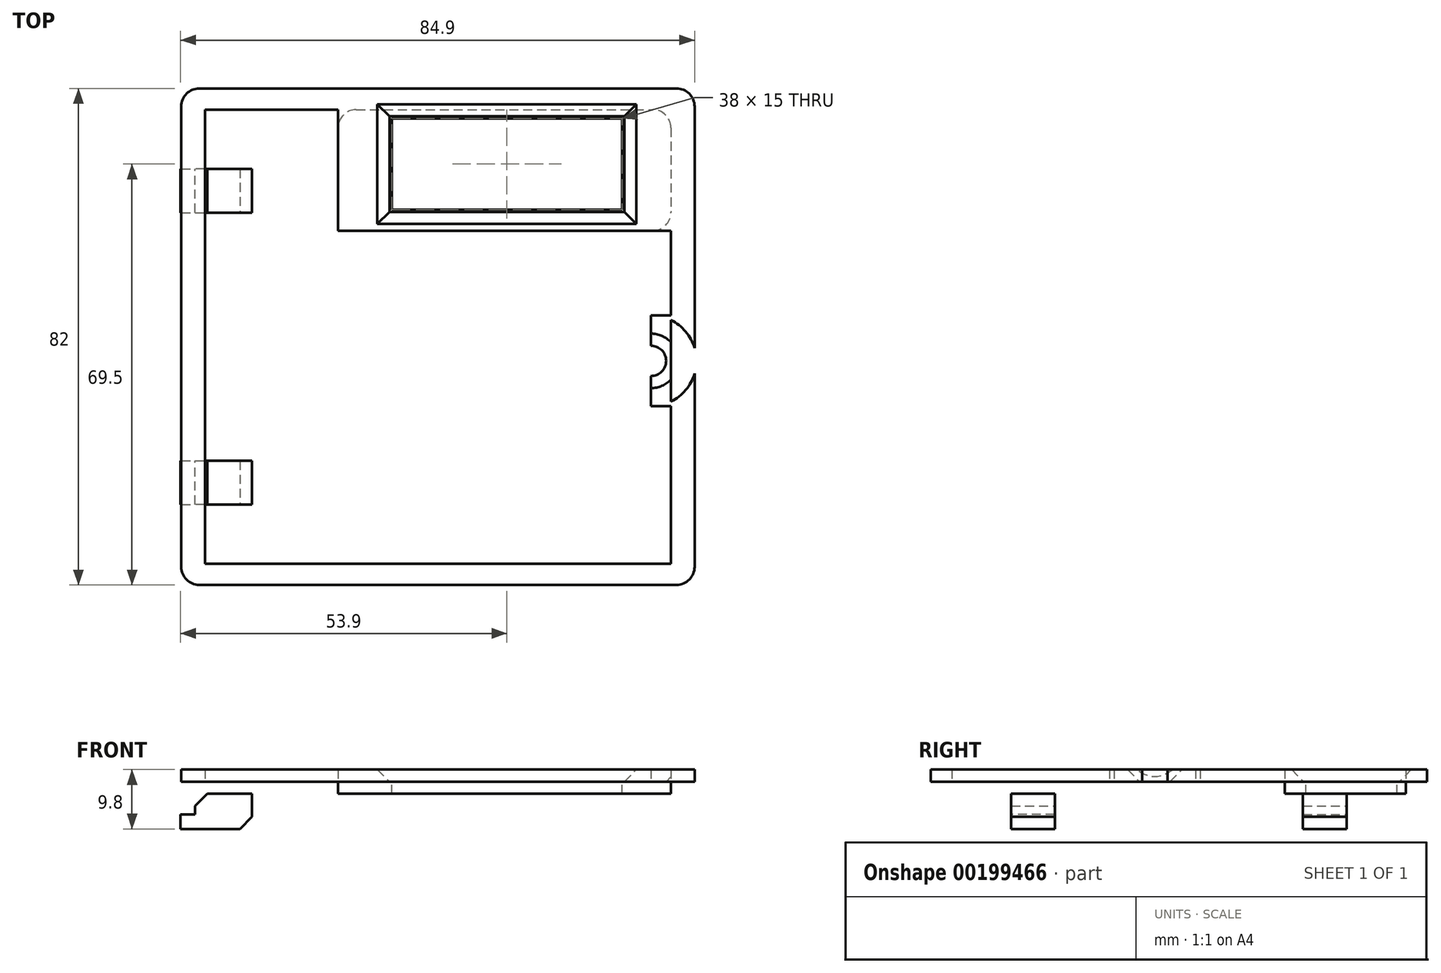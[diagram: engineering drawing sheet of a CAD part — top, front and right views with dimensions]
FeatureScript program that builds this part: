
annotation { "Feature Type Name" : "Feature", "Feature Type Description" : "" }
export const myFeature = defineFeature(function(context is Context, id is Id, definition is map)
    precondition{}
    {
        {
            var Q0;
            Q0=qCreatedBy(makeId("Top.planeOp"),FACE);
            var sketch = newSketch(context, id + "F0", { "sketchPlane" : qUnion([Q0])});
            skLineSegment(sketch, "E0.bottom", {"start": v(-34.8, 45) * mm, "end": v(50, 45) * mm});
            skLineSegment(sketch, "E0.top", {"start": v(-34.8, -37) * mm, "end": v(50, -37) * mm});
            skLineSegment(sketch, "E0.left", {"start": v(-34.8, 45) * mm, "end": v(-34.8, -37) * mm});
            skLineSegment(sketch, "E0.right", {"start": v(50, 45) * mm, "end": v(50, -37) * mm});
            skLineSegment(sketch, "E1.bottom", {"start": v(-30.9, 41.5) * mm, "end": v(46.1, 41.5) * mm});
            skLineSegment(sketch, "E1.top", {"start": v(-30.9, -33.5) * mm, "end": v(46.1, -33.5) * mm});
            skLineSegment(sketch, "E1.left", {"start": v(-30.9, 41.5) * mm, "end": v(-30.9, -33.5) * mm});
            skLineSegment(sketch, "E1.right", {"start": v(46.1, 41.5) * mm, "end": v(46.1, -33.5) * mm});
            skLineSegment(sketch, "E2.bottom", {"start": v(46.1, 41.5) * mm, "end": v(-8.9, 41.5) * mm});
            skLineSegment(sketch, "E2.top", {"start": v(46.1, 21.5) * mm, "end": v(-8.9, 21.5) * mm});
            skLineSegment(sketch, "E2.left", {"start": v(46.1, 41.5) * mm, "end": v(46.1, 21.5) * mm});
            skLineSegment(sketch, "E2.right", {"start": v(-8.9, 41.5) * mm, "end": v(-8.9, 21.5) * mm});
            skLineSegment(sketch, "E3.bottom", {"start": v(38, 40) * mm, "end": v(0, 40) * mm});
            skLineSegment(sketch, "E3.top", {"start": v(38, 25) * mm, "end": v(0, 25) * mm});
            skLineSegment(sketch, "E3.left", {"start": v(38, 40) * mm, "end": v(38, 25) * mm});
            skLineSegment(sketch, "E3.right", {"start": v(0, 40) * mm, "end": v(0, 25) * mm});
            skCircle(sketch, "E4", {"center": v(42.8, 0) * mm, "radius": 7.5 * mm});
            skCircle(sketch, "E5", {"center": v(42.8, 0) * mm, "radius": 1.5 * mm});
            skLineSegment(sketch, "E6.bottom", {"start": v(42.8, 7.5) * mm, "end": v(46.1, 7.5) * mm});
            skLineSegment(sketch, "E6.top", {"start": v(42.8, -7.5) * mm, "end": v(46.1, -7.5) * mm});
            skLineSegment(sketch, "E6.left", {"start": v(42.8, 7.5) * mm, "end": v(42.8, -7.5) * mm});
            skLineSegment(sketch, "E6.right", {"start": v(46.1, 7.5) * mm, "end": v(46.1, -7.5) * mm});
            skSolve(sketch);
        }
        {
            var Q0;
            Q0=makeQuery(id+"F0.imprint","IMPRINT",FACE,{"disambiguationData":[TD([[makeQuery(id+"F0.imprint","IMPRINT",EDGE,{"derivedFrom":sQuery(id+"F0.wireOp",EDGE,"E1.bottom")}),-1.0]])]});
            extrude(context, id + "F1", {"entities" : qUnion([Q0]), "oppositeDirection" : true, "depth" : 2 * mm});
        }
        {
            var Q0;
            Q0=makeQuery(id+"F1.opExtrude","SWEPT_EDGE",EDGE,{"disambiguationData":[OSD([sQuery(id+"F0.wireOp",EDGE,"E1.top"),sQuery(id+"F0.wireOp",EDGE,"E1.right")])]});
            var Q1;
            Q1=makeQuery(id+"F1.opExtrude","SWEPT_EDGE",EDGE,{"disambiguationData":[OSD([sQuery(id+"F0.wireOp",EDGE,"E1.bottom"),sQuery(id+"F0.wireOp",EDGE,"E1.right")])]});
            var Q2;
            Q2=makeQuery(id+"F1.opExtrude","SWEPT_EDGE",EDGE,{"disambiguationData":[OSD([sQuery(id+"F0.wireOp",EDGE,"E1.top"),sQuery(id+"F0.wireOp",EDGE,"E1.left")])]});
            var Q3;
            Q3=makeQuery(id+"F1.opExtrude","SWEPT_EDGE",EDGE,{"disambiguationData":[OSD([sQuery(id+"F0.wireOp",EDGE,"E1.bottom"),sQuery(id+"F0.wireOp",EDGE,"E1.left")])]});
            fillet(context, id + "F2", {"entities" : qUnion([Q0, Q1, Q2, Q3]), "radius" : 3 * mm, "tangentPropagation" : true, "allowEdgeOverflow" : false});
        }
        {
            var Q0;
            Q0=makeQuery(id+"F0.imprint","IMPRINT",FACE,{"disambiguationData":[TD([[makeQuery(id+"F0.imprint","IMPRINT",EDGE,{"derivedFrom":sQuery(id+"F0.wireOp",EDGE,"E2.bottom")}),1.0]])]});
            var Q1;
            Q1=makeQuery(id+"F0.imprint","IMPRINT",FACE,{"disambiguationData":[TD([[makeQuery(id+"F0.imprint","IMPRINT",EDGE,{"derivedFrom":sQuery(id+"F0.wireOp",EDGE,"E1.bottom")}),-1.0]])]});
            var Q2;
            {var subQ1=sQuery(id+"F0.wireOp",EDGE,"Ln5DI3G2-q5Om-ZSPF-1sAt-3ToPU1MPvuH6.right");var subQ3=sQuery(id+"F0.wireOp",EDGE,"FaX3msUC-2112-gFF6-oiMs-dLikajbDIMSI");var subQ4=makeQuery(id+"F0.imprint","INTERSECT",VERTEX,{"disambiguationData":[OD(0.0)],"derivedFrom":[subQ1,subQ3]});Q2=makeQuery(id+"F0.imprint","IMPRINT",FACE,{"disambiguationData":[TD([[makeQuery(id+"F0.imprint","IMPRINT",EDGE,{"disambiguationData":[TD([[subQ4,1.0]])],"derivedFrom":subQ3}),-1.0]])]});}
            var Q3;
            {var subQ0=sQuery(id+"F0.wireOp",EDGE,"Z5PLyE05-pE2t-pr7a-zb6Q-XgBUatr2Ev4L");var subQ3=sQuery(id+"F0.wireOp",EDGE,"Ln5DI3G2-q5Om-ZSPF-1sAt-3ToPU1MPvuH6.left");var subQ7=makeQuery(id+"F0.imprint","INTERSECT",VERTEX,{"disambiguationData":[OD(0.0)],"derivedFrom":[subQ3,subQ0]});Q3=makeQuery(id+"F0.imprint","IMPRINT",FACE,{"disambiguationData":[TD([[makeQuery(id+"F0.imprint","IMPRINT",EDGE,{"disambiguationData":[TD([[subQ7,-1.0]])],"derivedFrom":subQ3}),1.0]])]});}
            var Q4;
            {var subQ0=sQuery(id+"F0.wireOp",EDGE,"Z5PLyE05-pE2t-pr7a-zb6Q-XgBUatr2Ev4L");var subQ1=sQuery(id+"F0.wireOp",EDGE,"Ln5DI3G2-q5Om-ZSPF-1sAt-3ToPU1MPvuH6.left");var subQ2=makeQuery(id+"F0.imprint","INTERSECT",VERTEX,{"disambiguationData":[OD(0.0)],"derivedFrom":[subQ1,subQ0]});Q4=makeQuery(id+"F0.imprint","IMPRINT",FACE,{"disambiguationData":[TD([[makeQuery(id+"F0.imprint","IMPRINT",EDGE,{"disambiguationData":[TD([[subQ2,-1.0]])],"derivedFrom":subQ1}),-1.0]])]});}
            var Q5;
            {var subQ0=sQuery(id+"F0.wireOp",EDGE,"Ln5DI3G2-q5Om-ZSPF-1sAt-3ToPU1MPvuH6.bottom");Q5=makeQuery(id+"F0.imprint","IMPRINT",FACE,{"disambiguationData":[TD([[makeQuery(id+"F0.imprint","IMPRINT",EDGE,{"derivedFrom":subQ0}),-1.0]])]});}
            var Q6;
            {var subQ0=sQuery(id+"F0.wireOp",EDGE,"Ln5DI3G2-q5Om-ZSPF-1sAt-3ToPU1MPvuH6.top");Q6=makeQuery(id+"F0.imprint","IMPRINT",FACE,{"disambiguationData":[TD([[makeQuery(id+"F0.imprint","IMPRINT",EDGE,{"derivedFrom":subQ0}),1.0]])]});}
            var Q7;
            {var subQ0=sQuery(id+"F0.wireOp",EDGE,"E6.left");var subQ4=sQuery(id+"F0.wireOp",EDGE,"E5");var subQ5=makeQuery(id+"F0.imprint","INTERSECT",VERTEX,{"disambiguationData":[OD(0.0)],"derivedFrom":[subQ4,subQ0]});Q7=makeQuery(id+"F0.imprint","IMPRINT",FACE,{"disambiguationData":[TD([[makeQuery(id+"F0.imprint","IMPRINT",EDGE,{"disambiguationData":[TD([[subQ5,-1.0]])],"derivedFrom":subQ4}),-1.0]])]});}
            var Q8;
            {var subQ1=sQuery(id+"F0.wireOp",EDGE,"E6.bottom");var subQ2=sQuery(id+"F0.wireOp",EDGE,"E4");var subQ6=makeQuery(id+"F0.imprint","INTERSECT",VERTEX,{"derivedFrom":[subQ2,subQ1]});Q8=makeQuery(id+"F0.imprint","IMPRINT",FACE,{"disambiguationData":[TD([[makeQuery(id+"F0.imprint","IMPRINT",EDGE,{"disambiguationData":[TD([[subQ6,1.0]])],"derivedFrom":subQ2}),1.0]])]});}
            var Q9;
            {var subQ1=sQuery(id+"F0.wireOp",EDGE,"E6.top");Q9=makeQuery(id+"F0.imprint","IMPRINT",FACE,{"disambiguationData":[TD([[makeQuery(id+"F0.imprint","IMPRINT",EDGE,{"derivedFrom":subQ1}),1.0]])]});}
            var Q10;
            Q10=makeQuery(id+"F0.imprint","IMPRINT",FACE,{"disambiguationData":[TD([[makeQuery(id+"F0.imprint","IMPRINT",EDGE,{"derivedFrom":sQuery(id+"F0.wireOp",EDGE,"E0.bottom")}),-1.0]])]});
            var Q11;
            {var subQ0=sQuery(id+"F0.wireOp",EDGE,"E6.right");var subQ1=sQuery(id+"F0.wireOp",EDGE,"E4");var subQ2=makeQuery(id+"F0.imprint","INTERSECT",VERTEX,{"disambiguationData":[OD(0.0)],"derivedFrom":[subQ1,subQ0]});Q11=makeQuery(id+"F0.imprint","IMPRINT",FACE,{"disambiguationData":[TD([[makeQuery(id+"F0.imprint","IMPRINT",EDGE,{"disambiguationData":[TD([[subQ2,1.0]])],"derivedFrom":subQ1}),1.0]])]});}
            var Q12;
            {var subQ0=sQuery(id+"F0.wireOp",EDGE,"E6.bottom");Q12=makeQuery(id+"F0.imprint","IMPRINT",FACE,{"disambiguationData":[TD([[makeQuery(id+"F0.imprint","IMPRINT",EDGE,{"derivedFrom":subQ0}),-1.0]])]});}
            extrude(context, id + "F3", {"entities" : qUnion([Q0, Q1, Q2, Q3, Q4, Q5, Q6, Q7, Q8, Q9, Q10, Q11, Q12]), "depth" : 2 * mm});
        }
        {
            var Q0;
            Q0=makeQuery(id+"F3.opExtrude","SWEPT_EDGE",EDGE,{"disambiguationData":[OSD([sQuery(id+"F0.wireOp",EDGE,"E0.top"),sQuery(id+"F0.wireOp",EDGE,"E0.right")])]});
            var Q1;
            Q1=makeQuery(id+"F3.opExtrude","SWEPT_EDGE",EDGE,{"disambiguationData":[OSD([sQuery(id+"F0.wireOp",EDGE,"E0.top"),sQuery(id+"F0.wireOp",EDGE,"E0.left")])]});
            var Q2;
            Q2=makeQuery(id+"F3.opExtrude","SWEPT_EDGE",EDGE,{"disambiguationData":[OSD([sQuery(id+"F0.wireOp",EDGE,"E0.bottom"),sQuery(id+"F0.wireOp",EDGE,"E0.left")])]});
            var Q3;
            Q3=makeQuery(id+"F3.opExtrude","SWEPT_EDGE",EDGE,{"disambiguationData":[OSD([sQuery(id+"F0.wireOp",EDGE,"E0.bottom"),sQuery(id+"F0.wireOp",EDGE,"E0.right")])]});
            fillet(context, id + "F4", {"entities" : qUnion([Q0, Q1, Q2, Q3]), "radius" : 3 * mm, "tangentPropagation" : true, "allowEdgeOverflow" : false});
        }
        {
            var Q0;
            Q0=makeQuery(id+"F3.opExtrude","CAP_EDGE",EDGE,{"disambiguationData":[OSD([sQuery(id+"F0.wireOp",EDGE,"E3.bottom")])],"isStart":false});
            var Q1;
            Q1=makeQuery(id+"F3.opExtrude","CAP_EDGE",EDGE,{"disambiguationData":[OSD([sQuery(id+"F0.wireOp",EDGE,"E3.left")])],"isStart":false});
            var Q2;
            Q2=makeQuery(id+"F3.opExtrude","CAP_EDGE",EDGE,{"disambiguationData":[OSD([sQuery(id+"F0.wireOp",EDGE,"E3.top")])],"isStart":false});
            var Q3;
            Q3=makeQuery(id+"F3.opExtrude","CAP_EDGE",EDGE,{"disambiguationData":[OSD([sQuery(id+"F0.wireOp",EDGE,"E3.right")])],"isStart":false});
            chamfer(context, id + "F5", {"entities" : qUnion([Q0, Q1, Q2, Q3]), "width" : 2.4 * mm, "tangentPropagation" : true});
        }
        {
            var Q0;
            Q0=makeQuery(id+"F3.opExtrude","CAP_EDGE",EDGE,{"disambiguationData":[OSD([sQuery(id+"F0.wireOp",EDGE,"E5")])],"isStart":false});
            chamfer(context, id + "F6", {"entities" : qUnion([Q0]), "width" : 3 * mm, "tangentPropagation" : true});
        }
        {
            var Q0;
            Q0=qCreatedBy(makeId("Right.planeOp"),FACE);
            var sketch = newSketch(context, id + "F7", { "sketchPlane" : qUnion([Q0])});
            skLineSegment(sketch, "E7.bottom", {"start": v(-37.11, 0) * mm, "end": v(44.89, 0) * mm});
            skLineSegment(sketch, "E7.top", {"start": v(-37.11, -60) * mm, "end": v(44.89, -60) * mm});
            skLineSegment(sketch, "E7.left", {"start": v(-37.11, 0) * mm, "end": v(-37.11, -60) * mm});
            skLineSegment(sketch, "E7.right", {"start": v(44.89, 0) * mm, "end": v(44.89, -60) * mm});
            skLineSegment(sketch, "E8.bottom", {"start": v(24.49, -2) * mm, "end": v(31.69, -2) * mm});
            skLineSegment(sketch, "E8.top", {"start": v(24.49, -5.4) * mm, "end": v(31.69, -5.4) * mm});
            skLineSegment(sketch, "E8.left", {"start": v(24.49, -2) * mm, "end": v(24.49, -5.4) * mm});
            skLineSegment(sketch, "E8.right", {"start": v(31.69, -2) * mm, "end": v(31.69, -5.4) * mm});
            skLineSegment(sketch, "E9.top", {"start": v(24.49, -7.8) * mm, "end": v(31.69, -7.8) * mm});
            skLineSegment(sketch, "E9.left", {"start": v(24.49, -5.4) * mm, "end": v(24.49, -7.8) * mm});
            skLineSegment(sketch, "E9.right", {"start": v(31.69, -5.4) * mm, "end": v(31.69, -7.8) * mm});
            skLineSegment(sketch, "E10.bottom", {"start": v(-16.51, -2) * mm, "end": v(-23.71, -2) * mm});
            skLineSegment(sketch, "E10.top", {"start": v(-16.51, -5.4) * mm, "end": v(-23.71, -5.4) * mm});
            skLineSegment(sketch, "E10.left", {"start": v(-16.51, -2) * mm, "end": v(-16.51, -5.4) * mm});
            skLineSegment(sketch, "E10.right", {"start": v(-23.71, -2) * mm, "end": v(-23.71, -5.4) * mm});
            skLineSegment(sketch, "E11.top", {"start": v(-16.51, -7.8) * mm, "end": v(-23.71, -7.8) * mm});
            skLineSegment(sketch, "E11.left", {"start": v(-16.51, -5.4) * mm, "end": v(-16.51, -7.8) * mm});
            skLineSegment(sketch, "E11.right", {"start": v(-23.71, -5.4) * mm, "end": v(-23.71, -7.8) * mm});
            skSolve(sketch);
        }
        {
            var Q0;
            Q0=makeQuery(id+"F7.imprint","IMPRINT",FACE,{"disambiguationData":[TD([[makeQuery(id+"F7.imprint","IMPRINT",EDGE,{"derivedFrom":sQuery(id+"F7.wireOp",EDGE,"E8.bottom")}),-1.0]])]});
            var Q1;
            Q1=makeQuery(id+"F7.imprint","IMPRINT",FACE,{"disambiguationData":[TD([[makeQuery(id+"F7.imprint","IMPRINT",EDGE,{"derivedFrom":sQuery(id+"F7.wireOp",EDGE,"E10.bottom")}),1.0]])]});
            extrude(context, id + "F8", {"entities" : qUnion([Q0, Q1]), "operationType" : NewBodyOperationType.ADD, "oppositeDirection" : true, "depth" : 32.5 * mm, "hasSecondDirection" : true, "secondDirectionOppositeDirection" : true, "secondDirectionDepth" : 23.1 * mm});
        }
        {
            var Q0;
            Q0=makeQuery(id+"F7.imprint","IMPRINT",FACE,{"disambiguationData":[TD([[makeQuery(id+"F7.imprint","IMPRINT",EDGE,{"derivedFrom":sQuery(id+"F7.wireOp",EDGE,"E8.top")}),-1.0]])]});
            var Q1;
            Q1=makeQuery(id+"F7.imprint","IMPRINT",FACE,{"disambiguationData":[TD([[makeQuery(id+"F7.imprint","IMPRINT",EDGE,{"derivedFrom":sQuery(id+"F7.wireOp",EDGE,"E10.top")}),1.0]])]});
            extrude(context, id + "F9", {"entities" : qUnion([Q0, Q1]), "operationType" : NewBodyOperationType.ADD, "oppositeDirection" : true, "depth" : 34.9 * mm, "hasSecondDirection" : true, "secondDirectionOppositeDirection" : true, "secondDirectionDepth" : 23.1 * mm});
        }
        {
            var Q0;
            Q0=makeQuery(id+"F9.opExtrude","CAP_EDGE",EDGE,{"disambiguationData":[OSD([sQuery(id+"F7.wireOp",EDGE,"E11.top")])],"isStart":true});
            var Q1;
            Q1=makeQuery(id+"F9.opExtrude","CAP_EDGE",EDGE,{"disambiguationData":[OSD([sQuery(id+"F7.wireOp",EDGE,"E9.top")])],"isStart":true});
            chamfer(context, id + "F10", {"entities" : qUnion([Q0, Q1]), "width" : 2 * mm, "tangentPropagation" : true});
        }
        {
            var Q0;
            Q0=makeQuery(id+"F8.opExtrude","CAP_EDGE",EDGE,{"disambiguationData":[OSD([sQuery(id+"F7.wireOp",EDGE,"E10.bottom")])],"isStart":false});
            var Q1;
            Q1=makeQuery(id+"F8.opExtrude","CAP_EDGE",EDGE,{"disambiguationData":[OSD([sQuery(id+"F7.wireOp",EDGE,"E8.bottom")])],"isStart":false});
            chamfer(context, id + "F11", {"entities" : qUnion([Q0, Q1]), "width" : 2 * mm, "tangentPropagation" : true});
        }
    });
